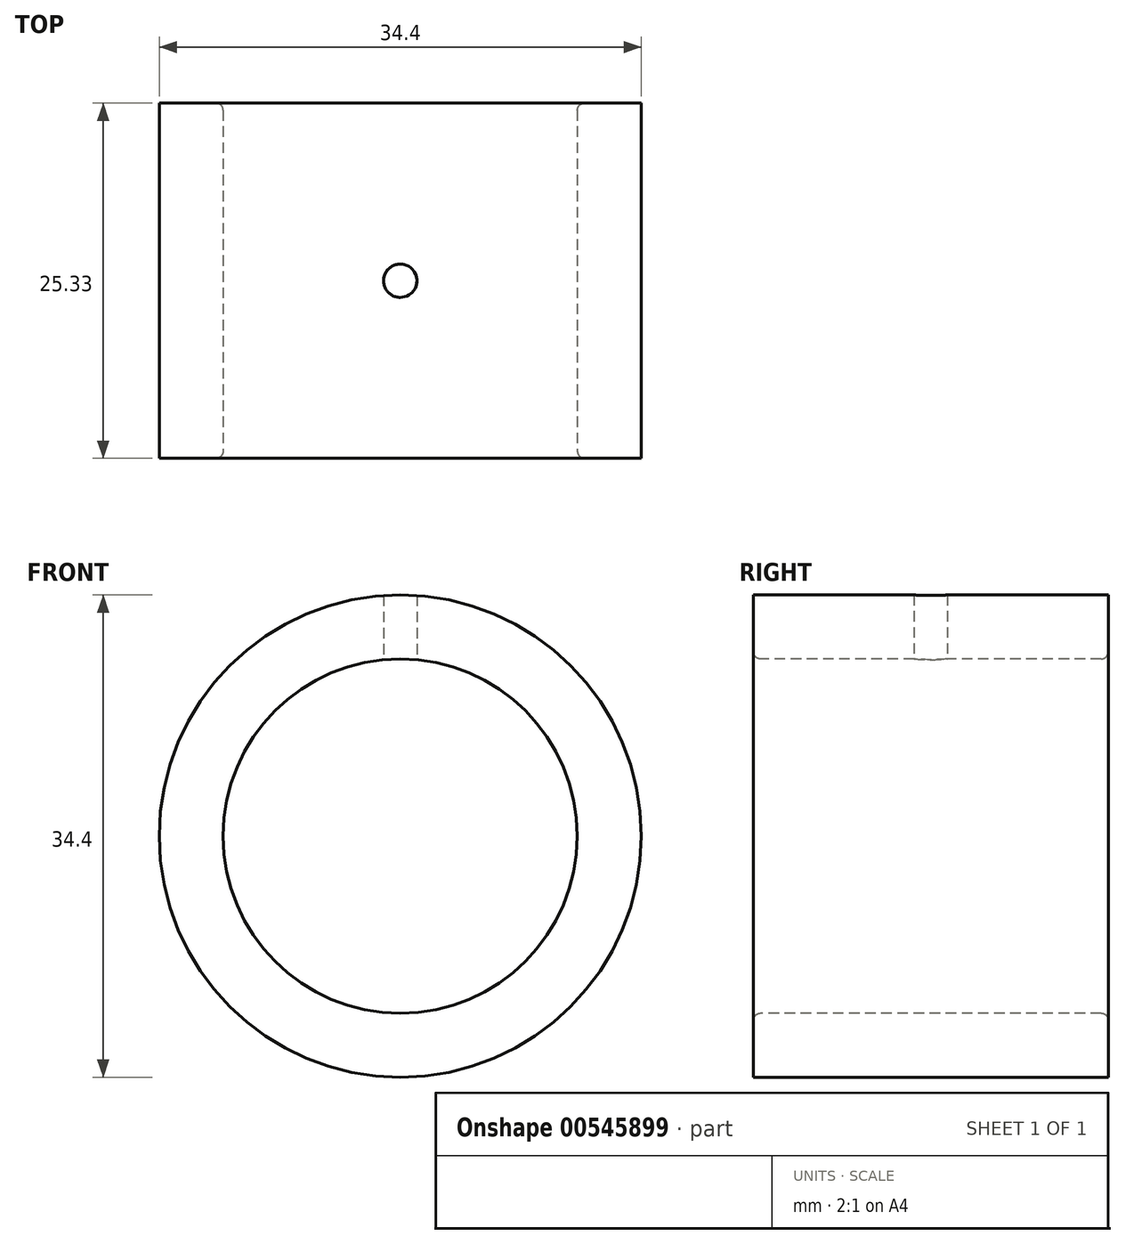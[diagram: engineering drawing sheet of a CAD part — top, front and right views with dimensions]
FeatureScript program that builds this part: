
annotation { "Feature Type Name" : "Feature", "Feature Type Description" : "" }
export const myFeature = defineFeature(function(context is Context, id is Id, definition is map)
    precondition{}
    {
        {
            var Q0;
            Q0=qCreatedBy(makeId("Top.planeOp"),FACE);
            var sketch = newSketch(context, id + "F0", { "sketchPlane" : qUnion([Q0])});
            skLineSegment(sketch, "E0", {"start": v(0, 0) * mm, "end": v(17.4, 0) * mm, "construction": true});
            skCircle(sketch, "E1", {"center": v(0, 0) * mm, "radius": 8.9 * mm, "construction": true});
            skLineSegment(sketch, "E2", {"start": v(17.4, 12.66) * mm, "end": v(13.14, 12.66) * mm});
            skLineSegment(sketch, "E3", {"start": v(17.4, -12.66) * mm, "end": v(13.14, -12.66) * mm});
            skLineSegment(sketch, "E4", {"start": v(0, -15.82) * mm, "end": v(0, 21.52) * mm, "construction": true});
            skLineSegment(sketch, "E5.0", {"start": v(17.4, -14.16) * mm, "end": v(11.14, -14.16) * mm});
            skLineSegment(sketch, "E5.2", {"start": v(17.4, 14.17) * mm, "end": v(11.14, 14.17) * mm});
            skLineSegment(sketch, "E6", {"start": v(17.4, 14.17) * mm, "end": v(17.4, 12.66) * mm});
            skLineSegment(sketch, "E7", {"start": v(17.4, -12.66) * mm, "end": v(17.4, -14.16) * mm});
            skLineSegment(sketch, "E8", {"start": v(11.14, 14.17) * mm, "end": v(11.14, -14.16) * mm});
            skLineSegment(sketch, "E9", {"start": v(12.64, 12.16) * mm, "end": v(12.64, -12.16) * mm});
            skPoint(sketch, "E10.visualSharp", {"position": v(12.64, 12.66) * mm});
            skArc(sketch, "E10.filletArc", {"start": v(13.14, 12.66) * mm, "mid": v(12.78, 12.52) * mm, "end": v(12.64, 12.16) * mm});
            skPoint(sketch, "E11.visualSharp", {"position": v(12.64, -12.66) * mm});
            skArc(sketch, "E11.filletArc", {"start": v(12.64, -12.16) * mm, "mid": v(12.78, -12.5) * mm, "end": v(13.14, -12.66) * mm});
            skPoint(sketch, "E12.visualSharp", {"position": v(11.14, 14.17) * mm});
            skPoint(sketch, "E13.visualSharp", {"position": v(11.14, -14.16) * mm});
            skSolve(sketch);
        }
        {
            var Q0;
            Q0=qSketchRegion(id+"F0",true);
            var Q1;
            Q1=sQuery(id+"F0.wireOp",EDGE,"E4");
            revolve(context, id + "F1", {"entities" : qUnion([Q0]), "axis" : qUnion([Q1]), "revolveType" : RevolveType.FULL});
        }
        {
            var Q0;
            Q0=qCreatedBy(makeId("Front.planeOp"),FACE);
            var sketch = newSketch(context, id + "F2", { "sketchPlane" : qUnion([Q0])});
            skCircle(sketch, "E14.0", {"center": v(0, 0) * mm, "radius": 12.64 * mm});
            skCircle(sketch, "E15.0", {"center": v(0, 0) * mm, "radius": 17.4 * mm, "construction": true});
            skCircle(sketch, "E16", {"center": v(0, 0) * mm, "radius": 17.2 * mm});
            skSolve(sketch);
        }
        {
            var Q0;
            Q0 = qSketchRegion(id + "F2", true);
            extrude(context, id + "F3", {"entities" : qUnion([Q0]), "endBound" : BoundingType.UP_TO_NEXT, "oppositeDirection" : true, "depth" : 25.4 * mm, "offsetDistance" : 25.4 * mm, "hasSecondDirection" : true, "secondDirectionBound" : SecondDirectionBoundingType.UP_TO_NEXT, "secondDirectionOppositeDirection" : false, "secondDirectionDepth" : 25.4 * mm});
        }
        {
            var Q0;
            Q0=makeQuery(id+"F1.opRevolve","SWEPT_BODY",BODY,{"disambiguationData":[OSD([sQuery(id+"F0.wireOp",EDGE,"E2"),sQuery(id+"F0.wireOp",EDGE,"E3"),sQuery(id+"F0.wireOp",EDGE,"E5.0"),sQuery(id+"F0.wireOp",EDGE,"E5.2"),sQuery(id+"F0.wireOp",EDGE,"E6"),sQuery(id+"F0.wireOp",EDGE,"E7"),sQuery(id+"F0.wireOp",EDGE,"E8"),sQuery(id+"F0.wireOp",EDGE,"E9"),sQuery(id+"F0.wireOp",EDGE,"E10.filletArc"),sQuery(id+"F0.wireOp",EDGE,"E11.filletArc")])]});
            var Q1;
            Q1=makeQuery(id+"F3.opExtrude","SWEPT_BODY",BODY,{"disambiguationData":[OSD([sQuery(id+"F2.wireOp",EDGE,"E14.0"),sQuery(id+"F2.wireOp",EDGE,"E15.0")])]});
            booleanBodies(context, id + "F4", {"operationType" : BooleanOperationType.SUBTRACTION, "tools" : qUnion([Q0]), "targets" : qUnion([Q1])});
        }
        {
            var Q0;
            Q0=qCreatedBy(makeId("Top.planeOp"),FACE);
            var sketch = newSketch(context, id + "F5", { "sketchPlane" : qUnion([Q0])});
            skCircle(sketch, "E17", {"center": v(0, 0) * mm, "radius": 1.2 * mm});
            skSolve(sketch);
        }
        {
            var Q0;
            Q0 = qSketchRegion(id + "F5", true);
            extrude(context, id + "F6", {"entities" : qUnion([Q0]), "operationType" : NewBodyOperationType.REMOVE, "endBound" : BoundingType.THROUGH_ALL, "depth" : 25.4 * mm, "offsetDistance" : 25.4 * mm});
        }
    });
